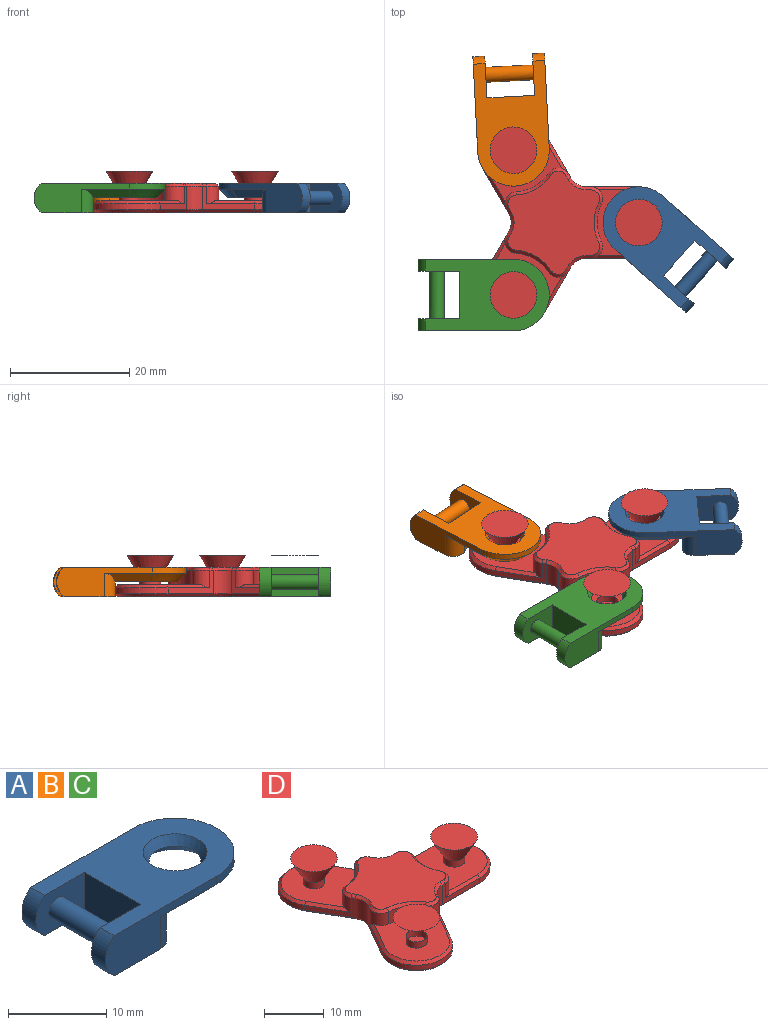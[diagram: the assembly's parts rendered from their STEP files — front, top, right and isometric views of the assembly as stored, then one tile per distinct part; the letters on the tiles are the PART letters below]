
ASSEMBLY  parts=4 mates=3
PART A: 20 faces, bbox 22x12x5 mm
  f0: plane 16x5mm, normal (0,1,0), area 45.9mm2, adj f3,f4,f6,f9,f13,f18
  f1: plane 7x5mm, normal (0,-1,0), area 28.2mm2, adj f3,f4,f7,f9,f10
  f2: plane 7x5mm, normal (0,1,0), area 28.2mm2, adj f3,f4,f7,f8,f10
  f3: plane 20.75x12mm, normal (0,0,1), area 154.4mm2, adj f0,f1,f2,f5,f6,f7,f8,f9
  f4: plane 12x8.69mm, normal (0,0,-1), area 52.1mm2, adj f0,f1,f2,f5,f7,f8,f9,f11
  f5: plane 16x5mm, normal (0,-1,0), area 45.9mm2, adj f3,f4,f6,f8,f11,f16
  f6: cylinder r=6mm len=12mm, axis (0,0,-1), area 18.8mm2, adj f0,f3,f5,f17
  f7: plane 8x5mm, normal (-1,0,0), area 40mm2, adj f1,f2,f3,f4
  f8: cylinder r=3.12mm len=5mm, axis (0,-1,0), area 11.6mm2, adj f2,f3,f4,f5
  f9: cylinder r=3.12mm len=5mm, axis (0,-1,0), area 11.6mm2, adj f0,f1,f3,f4
  f10: cylinder r=1.25mm len=8mm, axis (0,-1,0), area 62.8mm2, adj f1,f2
  f11: cylinder r=2mm len=4mm, axis (0,0,-1), area 12.7mm2, adj f4,f5,f12,f14,f16
  f12: cylinder r=7mm len=6.22mm, axis (0,0,-1), area 16.1mm2, adj f4,f11,f13,f14
  f13: cylinder r=2mm len=4mm, axis (0,0,-1), area 12.7mm2, adj f0,f4,f12,f14,f18
  f14: plane 11.5x9mm, normal (0,0,-1), area 40.1mm2, adj f11,f12,f13,f16,f17,f18,f19
  f15: cone r=3.25mm half-angle=30deg, axis (0,0,1), area 23.4mm2, adj f3,f19
  f16: plane 8.06x1.5mm, normal (0,-0.71,-0.71), area 14.1mm2, adj f5,f11,f14,f17
  f17: cone r=6mm half-angle=45deg, axis (0,0,1), area 35mm2, adj f6,f14,f16,f18
  f18: plane 8.06x1.5mm, normal (0,0.71,-0.71), area 14.1mm2, adj f0,f13,f14,f17
  f19: cone r=2.52mm half-angle=45deg, axis (0,0,-1), area 41.3mm2, adj f14,f15
PART B: same geometry as A
PART C: same geometry as A
PART D: 74 faces, bbox 33x36.2x7 mm
  f0: plane 8.8x4mm, normal (0,1,0), area 11mm2, adj f1,f6,f32,f38,f46,f59
  f1: cylinder r=6mm len=12mm, axis (0,0,-1), area 18.8mm2, adj f0,f3,f39,f44
  f2: plane 17.28x15.37mm, normal (0,0,1), area 178.3mm2, adj f56,f57,f58,f59,f60,f61,f62,f63
  f3: plane 8.8x4mm, normal (0,-1,0), area 11mm2, adj f1,f5,f33,f40,f45,f60
  f4: plane 35.25x32mm, normal (0,0,-1), area 554.1mm2, adj f44,f45,f46,f47,f48,f49,f50,f51
  f5: cylinder r=2mm len=3mm, axis (0,0,1), area 10.6mm2, adj f3,f8,f9,f40,f58
  f6: cylinder r=2mm len=3mm, axis (0,0,1), area 10.6mm2, adj f0,f8,f9,f38,f57
  f7: cylinder r=1.75mm len=3.5mm, axis (0,0,1), area 13.9mm2, adj f9,f10
  f8: cylinder r=7mm len=6.22mm, axis (0,0,1), area 16.1mm2, adj f5,f6,f9,f56
  f9: plane 12.5x11mm, normal (0,0,1), area 109.7mm2, adj f5,f6,f7,f8,f38,f39,f40
  f10: cone r=2.75mm half-angle=30deg, axis (0,0,1), area 76.6mm2, adj f7,f11
  f11: plane 7.81x7.81mm, normal (0,0,1), area 47.9mm2, adj f10
  f12: plane 7.62x4.4mm, normal (0.87,-0.5,0), area 11mm2, adj f23,f26,f33,f35,f49,f64
  f13: plane 7.62x4.4mm, normal (-0.87,-0.5,0), area 11mm2, adj f14,f17,f34,f41,f54,f71
  f14: cylinder r=6mm len=11.2mm, axis (0,0,-1), area 18.8mm2, adj f13,f15,f42,f52
  f15: plane 7.62x4.4mm, normal (0.87,0.5,0), area 11mm2, adj f14,f16,f32,f43,f50,f63
  f16: cylinder r=2mm len=3.4mm, axis (0,0,1), area 10.6mm2, adj f15,f19,f20,f43,f65
  f17: cylinder r=2mm len=3mm, axis (0,0,1), area 10.6mm2, adj f13,f19,f20,f41,f69
  f18: cylinder r=1.75mm len=3.5mm, axis (0,0,1), area 13.9mm2, adj f20,f21
  f19: cylinder r=7mm len=5.39mm, axis (0,0,1), area 16.1mm2, adj f16,f17,f20,f67
  f20: plane 14.09x13.63mm, normal (0,0,1), area 109.7mm2, adj f16,f17,f18,f19,f41,f42,f43
  f21: cone r=2.75mm half-angle=30deg, axis (0,0,1), area 76.6mm2, adj f18,f22
  f22: plane 7.81x7.81mm, normal (0,0,1), area 47.9mm2, adj f21
  f23: cylinder r=6mm len=11.2mm, axis (0,0,-1), area 18.8mm2, adj f12,f24,f36,f51
  f24: plane 7.62x4.4mm, normal (-0.87,0.5,0), area 11mm2, adj f23,f25,f34,f37,f53,f72
  f25: cylinder r=2mm len=3mm, axis (0,0,1), area 10.6mm2, adj f24,f28,f29,f37,f70
  f26: cylinder r=2mm len=3.4mm, axis (0,0,1), area 10.6mm2, adj f12,f28,f29,f35,f66
  f27: cylinder r=1.75mm len=3.5mm, axis (0,0,1), area 13.9mm2, adj f29,f30
  f28: cylinder r=7mm len=5.39mm, axis (0,0,1), area 16.1mm2, adj f25,f26,f29,f68
  f29: plane 14.09x13.63mm, normal (0,0,1), area 109.7mm2, adj f25,f26,f27,f28,f35,f36,f37
  f30: cone r=2.75mm half-angle=30deg, axis (0,0,1), area 76.6mm2, adj f27,f31
  f31: plane 7.81x7.81mm, normal (0,0,1), area 47.9mm2, adj f30
  f32: cylinder r=3mm len=4mm, axis (0,0,1), area 12.6mm2, adj f0,f15,f48,f61
  f33: cylinder r=3mm len=4mm, axis (0,0,-1), area 12.6mm2, adj f3,f12,f47,f62
  f34: cylinder r=3mm len=4mm, axis (0,0,1), area 12.6mm2, adj f13,f24,f55,f73
  f35: plane 6.98x4.46mm, normal (0.61,-0.35,0.71), area 5.1mm2, adj f12,f26,f29,f36
  f36: cone r=5.5mm half-angle=45deg, axis (0,0,-1), area 12.8mm2, adj f23,f29,f35,f37
  f37: plane 7.23x4.03mm, normal (-0.61,0.35,0.71), area 5.1mm2, adj f24,f25,f29,f36
  f38: plane 8.06x0.5mm, normal (0,0.71,0.71), area 5.1mm2, adj f0,f6,f9,f39
  f39: cone r=5.5mm half-angle=45deg, axis (0,0,-1), area 12.8mm2, adj f1,f9,f38,f40
  f40: plane 8.06x0.5mm, normal (0,-0.71,0.71), area 5.1mm2, adj f3,f5,f9,f39
  f41: plane 7.23x4.03mm, normal (-0.61,-0.35,0.71), area 5.1mm2, adj f13,f17,f20,f42
  f42: cone r=5.5mm half-angle=45deg, axis (0,0,-1), area 12.8mm2, adj f14,f20,f41,f43
  f43: plane 6.98x4.46mm, normal (0.61,0.35,0.71), area 5.1mm2, adj f15,f16,f20,f42
  f44: cone r=6mm half-angle=45deg, axis (0,0,1), area 12.8mm2, adj f1,f4,f45,f46
  f45: plane 8.8x0.5mm, normal (0,-0.71,-0.71), area 6.2mm2, adj f3,f4,f44,f47
  f46: plane 8.8x0.5mm, normal (0,0.71,-0.71), area 6.2mm2, adj f0,f4,f44,f48
  f47: cone r=3.5mm half-angle=45deg, axis (0,0,-1), area 2.4mm2, adj f4,f33,f45,f49
  f48: cone r=3.5mm half-angle=45deg, axis (0,0,-1), area 2.4mm2, adj f4,f32,f46,f50
  f49: plane 7.87x4.84mm, normal (0.61,-0.35,-0.71), area 6.2mm2, adj f4,f12,f47,f51
  f50: plane 7.87x4.84mm, normal (0.61,0.35,-0.71), area 6.2mm2, adj f4,f15,f48,f52
  f51: cone r=6mm half-angle=45deg, axis (0,0,1), area 12.8mm2, adj f4,f23,f49,f53
  f52: cone r=6mm half-angle=45deg, axis (0,0,1), area 12.8mm2, adj f4,f14,f50,f54
  f53: plane 7.87x4.84mm, normal (-0.61,0.35,-0.71), area 6.2mm2, adj f4,f24,f51,f55
  f54: plane 7.87x4.84mm, normal (-0.61,-0.35,-0.71), area 6.2mm2, adj f4,f13,f52,f55
  f55: cone r=3.5mm half-angle=45deg, axis (0,0,-1), area 2.4mm2, adj f4,f34,f53,f54
  f56: cone r=7mm half-angle=45deg, axis (0,0,1), area 4.7mm2, adj f2,f8,f57,f58
  f57: cone r=1.5mm half-angle=45deg, axis (0,0,-1), area 2.5mm2, adj f2,f6,f56,f59
  f58: cone r=1.5mm half-angle=45deg, axis (0,0,-1), area 2.5mm2, adj f2,f5,f56,f60
  f59: plane 0.74x0.5mm, normal (0,0.71,0.71), area 0.5mm2, adj f0,f2,f57,f61
  f60: plane 0.74x0.5mm, normal (0,-0.71,0.71), area 0.5mm2, adj f2,f3,f58,f62
  f61: cone r=3.5mm half-angle=45deg, axis (0,0,1), area 2.4mm2, adj f2,f32,f59,f63
  f62: cone r=3.5mm half-angle=45deg, axis (0,0,1), area 2.4mm2, adj f2,f33,f60,f64
  f63: plane 0.89x0.8mm, normal (0.61,0.35,0.71), area 0.5mm2, adj f2,f15,f61,f65
  f64: plane 0.89x0.8mm, normal (0.61,-0.35,0.71), area 0.5mm2, adj f2,f12,f62,f66
  f65: cone r=1.5mm half-angle=45deg, axis (0,0,-1), area 2.5mm2, adj f2,f16,f63,f67
  f66: cone r=1.5mm half-angle=45deg, axis (0,0,-1), area 2.5mm2, adj f2,f26,f64,f68
  f67: cone r=7mm half-angle=45deg, axis (0,0,1), area 4.7mm2, adj f2,f19,f65,f69
  f68: cone r=7mm half-angle=45deg, axis (0,0,1), area 4.7mm2, adj f2,f28,f66,f70
  f69: cone r=1.5mm half-angle=45deg, axis (0,0,-1), area 2.5mm2, adj f2,f17,f67,f71
  f70: cone r=1.5mm half-angle=45deg, axis (0,0,-1), area 2.5mm2, adj f2,f25,f68,f72
  f71: plane 0.89x0.8mm, normal (-0.61,-0.35,0.71), area 0.5mm2, adj f2,f13,f69,f73
  f72: plane 0.89x0.8mm, normal (-0.61,0.35,0.71), area 0.5mm2, adj f2,f24,f70,f73
  f73: cone r=3.5mm half-angle=45deg, axis (0,0,1), area 2.4mm2, adj f2,f34,f71,f72
PLACE A rot(axis=(0,0,1),138.4deg) t=(33.53,30.71,-46.93)mm
PLACE B rot(axis=(0,0,-1),87.1deg) t=(107.04,56.57,-46.93)mm
PLACE C t=(72.37,94.66,-46.93)mm
PLACE D t=(114.86,83.56,-46.93)mm fixed
MATE revolute D.f23 <-> C.f6  axis (0,0,1) through (56.91,45.25,-39.93)mm
MATE revolute D.f1 <-> A.f6  axis (0,0,1) through (77.91,57.37,-39.93)mm
MATE revolute D.f14 <-> B.f6  axis (0,0,1) through (56.91,69.5,-39.93)mm
